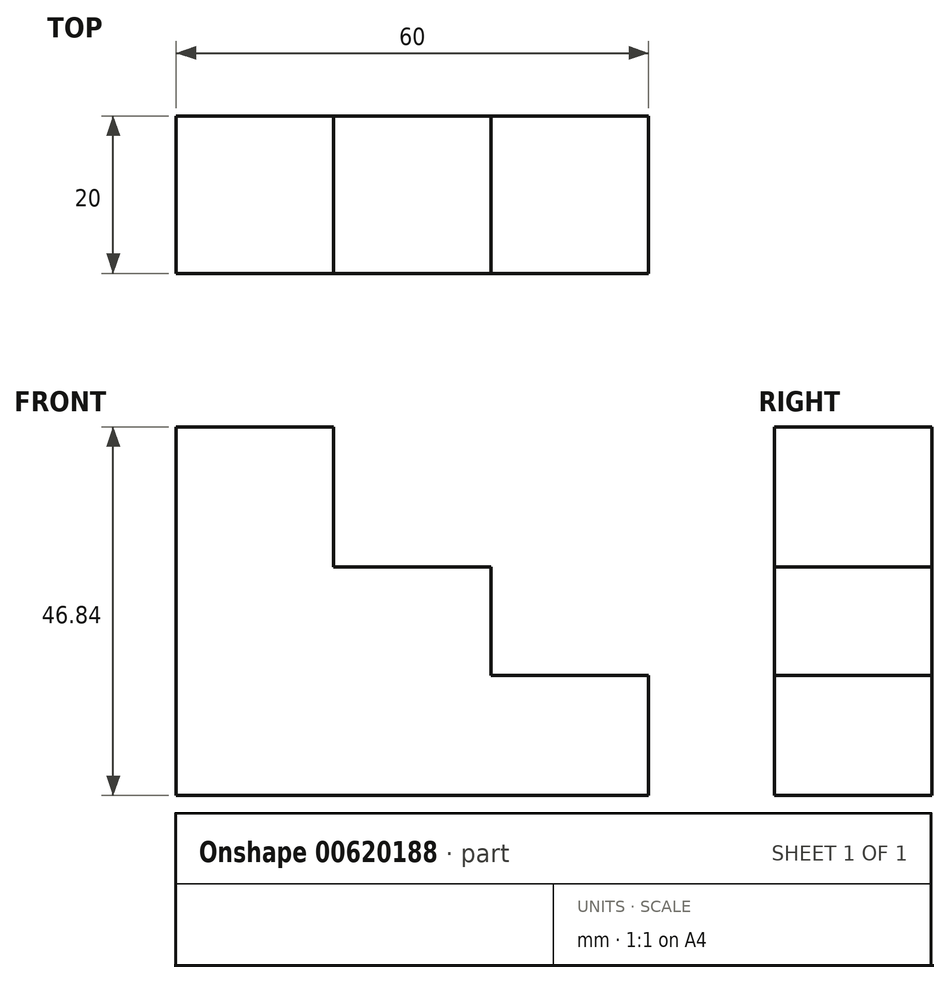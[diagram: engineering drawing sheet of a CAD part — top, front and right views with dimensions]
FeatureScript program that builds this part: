
annotation { "Feature Type Name" : "Feature", "Feature Type Description" : "" }
export const myFeature = defineFeature(function(context is Context, id is Id, definition is map)
    precondition{}
    {
        {
            var Q0;
            Q0=qCreatedBy(makeId("Front.planeOp"),FACE);
            var sketch = newSketch(context, id + "F0", { "sketchPlane" : qUnion([Q0])});
            skLineSegment(sketch, "E0", {"start": v(-64.82, 51.34) * mm, "end": v(-64.82, 30.09) * mm});
            skLineSegment(sketch, "E1", {"start": v(-64.82, 51.34) * mm, "end": v(-44.82, 51.34) * mm});
            skLineSegment(sketch, "E2", {"start": v(-44.82, 51.34) * mm, "end": v(-44.82, 33.52) * mm});
            skLineSegment(sketch, "E3", {"start": v(-44.82, 33.52) * mm, "end": v(-24.82, 33.52) * mm});
            skLineSegment(sketch, "E4", {"start": v(-24.82, 33.52) * mm, "end": v(-24.82, 19.8) * mm});
            skLineSegment(sketch, "E5", {"start": v(-24.82, 19.8) * mm, "end": v(-4.82, 19.8) * mm});
            skLineSegment(sketch, "E6", {"start": v(-4.82, 19.8) * mm, "end": v(-4.82, 4.5) * mm});
            skLineSegment(sketch, "E7", {"start": v(-4.82, 4.5) * mm, "end": v(-64.82, 4.5) * mm});
            skLineSegment(sketch, "E8", {"start": v(-64.82, 4.5) * mm, "end": v(-64.82, 30.09) * mm});
            skSolve(sketch);
        }
        {
            var Q0;
            Q0 = qSketchRegion(id + "F0", true);
            extrude(context, id + "F1", {"entities" : qUnion([Q0]), "depth" : 20 * mm, "offsetDistance" : 25 * mm});
        }
    });
